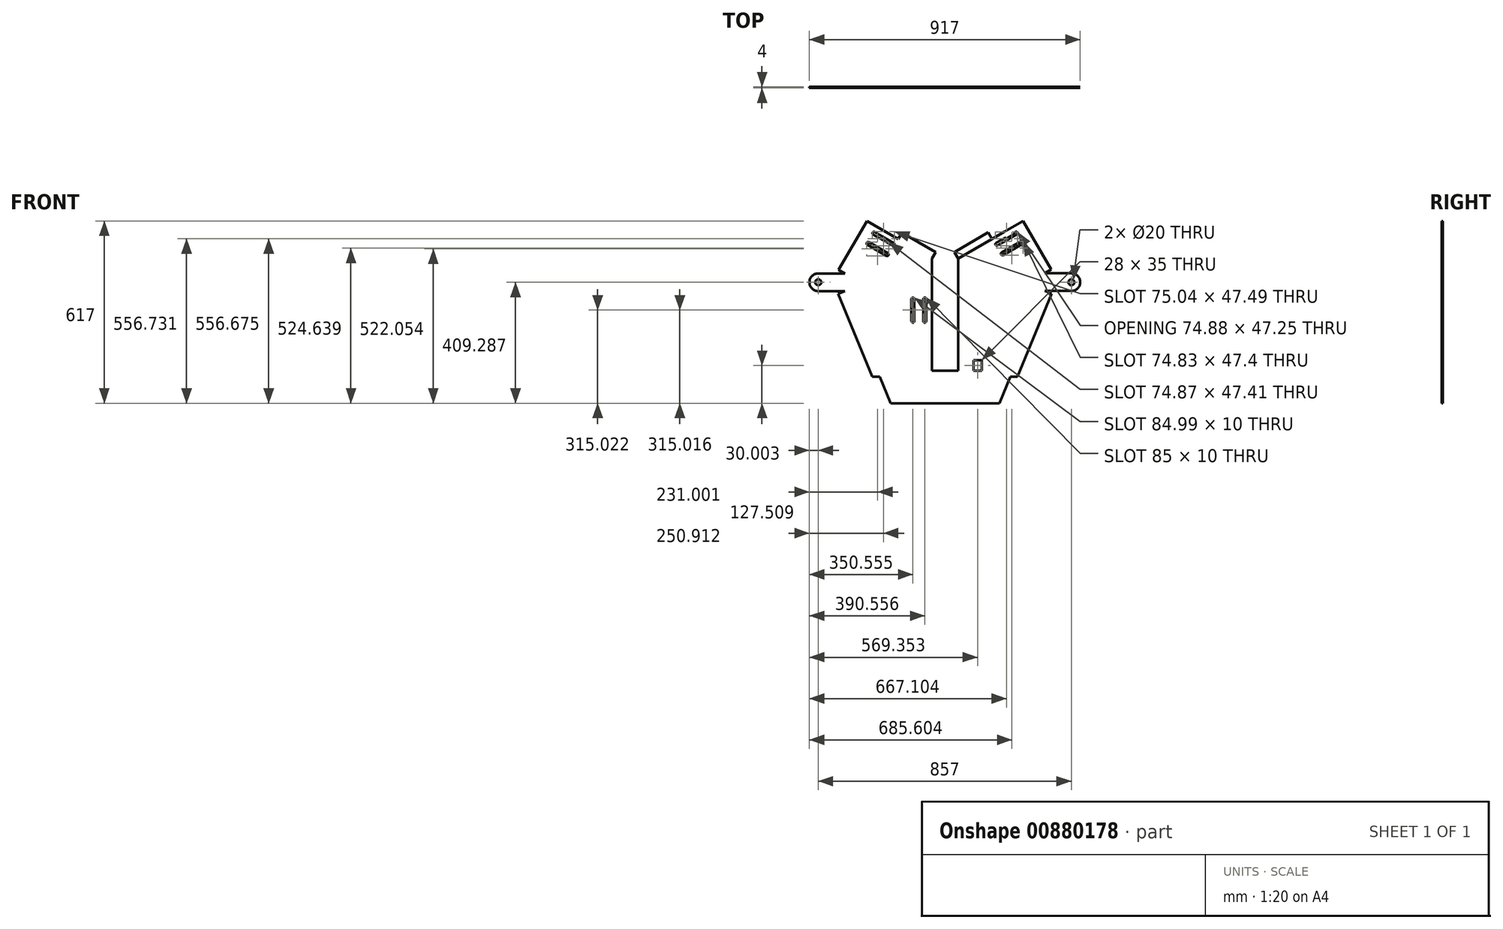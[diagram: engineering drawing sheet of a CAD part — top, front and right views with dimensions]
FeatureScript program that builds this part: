
annotation { "Feature Type Name" : "Feature", "Feature Type Description" : "" }
export const myFeature = defineFeature(function(context is Context, id is Id, definition is map)
    precondition{}
    {
        {
            var Q0;
            Q0=qCreatedBy(makeId("Front.planeOp"),FACE);
            var sketch = newSketch(context, id + "F0", { "sketchPlane" : qUnion([Q0])});
            skLineSegment(sketch, "E0", {"start": v(-22.56, -280.39) * mm, "end": v(-22.56, 69.61) * mm});
            skLineSegment(sketch, "E1", {"start": v(66.44, 119.61) * mm, "end": v(66.44, -280.39) * mm});
            skLineSegment(sketch, "E2", {"start": v(-174.12, 207.1) * mm, "end": v(-224.12, 120.5) * mm});
            skCircle(sketch, "E3", {"center": v(-218.75, 205.12) * mm, "radius": 5 * mm});
            skCircle(sketch, "E4", {"center": v(-153.63, 167.56) * mm, "radius": 5 * mm});
            skCircle(sketch, "E5", {"center": v(-238.59, 170.41) * mm, "radius": 5 * mm});
            skCircle(sketch, "E6", {"center": v(-173.63, 132.91) * mm, "radius": 5 * mm});
            skLineSegment(sketch, "E7", {"start": v(-171.13, 137.24) * mm, "end": v(-236.09, 174.74) * mm});
            skLineSegment(sketch, "E8", {"start": v(-241.09, 166.08) * mm, "end": v(-176.13, 128.58) * mm});
            skCircle(sketch, "E9", {"center": v(-46.56, -17.87) * mm, "radius": 5 * mm});
            skCircle(sketch, "E10", {"center": v(-46.56, -92.87) * mm, "radius": 5 * mm});
            skLineSegment(sketch, "E11", {"start": v(-51.55, -93.04) * mm, "end": v(-51.55, -17.7) * mm});
            skCircle(sketch, "E12", {"center": v(-86.56, -17.87) * mm, "radius": 5 * mm});
            skCircle(sketch, "E13", {"center": v(-86.56, -92.87) * mm, "radius": 5 * mm});
            skLineSegment(sketch, "E14", {"start": v(-81.6, -93.57) * mm, "end": v(-81.56, -17.87) * mm});
            skLineSegment(sketch, "E15", {"start": v(-91.56, -17.87) * mm, "end": v(-91.56, -92.87) * mm});
            skLineSegment(sketch, "E16", {"start": v(-41.56, -17.95) * mm, "end": v(-41.56, -92.7) * mm});
            skCircle(sketch, "E17", {"center": v(197.5, 167.6) * mm, "radius": 5 * mm});
            skCircle(sketch, "E18", {"center": v(262.46, 205.1) * mm, "radius": 5 * mm});
            skLineSegment(sketch, "E19", {"start": v(265.1, 200.86) * mm, "end": v(199.86, 163.19) * mm});
            skCircle(sketch, "E20", {"center": v(216.04, 135.5) * mm, "radius": 5 * mm});
            skCircle(sketch, "E21", {"center": v(281, 173) * mm, "radius": 5 * mm});
            skLineSegment(sketch, "E22", {"start": v(279.12, 177.65) * mm, "end": v(213.54, 139.84) * mm});
            skLineSegment(sketch, "E23", {"start": v(218.54, 131.18) * mm, "end": v(283.5, 168.68) * mm});
            skLineSegment(sketch, "E24", {"start": v(195.07, 171.97) * mm, "end": v(259.82, 209.34) * mm});
            skLineSegment(sketch, "E25", {"start": v(-102.56, -370.39) * mm, "end": v(146.44, -370.39) * mm});
            skLineSegment(sketch, "E26", {"start": v(359.9, 69.35) * mm, "end": v(359.9, 9.35) * mm});
            skLineSegment(sketch, "E27", {"start": v(-22.56, -260.39) * mm, "end": v(66.44, -260.39) * mm});
            skLineSegment(sketch, "E28", {"start": v(-22.56, 69.61) * mm, "end": v(-22.56, 119.61) * mm});
            skLineSegment(sketch, "E29", {"start": v(-177.57, 209.11) * mm, "end": v(-22.56, 119.61) * mm});
            skLineSegment(sketch, "E30", {"start": v(-22.56, 119.61) * mm, "end": v(66.44, 119.61) * mm});
            skLineSegment(sketch, "E31", {"start": v(-22.56, 119.61) * mm, "end": v(21.94, 196.69) * mm});
            skLineSegment(sketch, "E32", {"start": v(21.94, 196.69) * mm, "end": v(66.44, 119.61) * mm});
            skLineSegment(sketch, "E33", {"start": v(-0.3, 158.15) * mm, "end": v(66.44, 119.61) * mm});
            skLineSegment(sketch, "E34", {"start": v(44.2, 158.15) * mm, "end": v(-22.56, 119.61) * mm});
            skLineSegment(sketch, "E35", {"start": v(21.94, 119.61) * mm, "end": v(21.94, 196.69) * mm});
            skCircle(sketch, "E36", {"center": v(21.94, 145.3) * mm, "radius": 36.15 * mm});
            skLineSegment(sketch, "E37", {"start": v(-22.56, 119.61) * mm, "end": v(-174.1, 207.11) * mm});
            skLineSegment(sketch, "E38", {"start": v(-177.57, 209.11) * mm, "end": v(-220.88, 234.11) * mm});
            skLineSegment(sketch, "E39", {"start": v(-220.88, 234.11) * mm, "end": v(-317.1, 68.9) * mm, "construction": true});
            skLineSegment(sketch, "E40", {"start": v(146.44, -370.39) * mm, "end": v(206.44, -370.39) * mm});
            skLineSegment(sketch, "E41", {"start": v(-102.56, -370.39) * mm, "end": v(-162.56, -370.39) * mm});
            skLineSegment(sketch, "E42", {"start": v(66.44, 119.61) * mm, "end": v(221.46, 209.11) * mm});
            skLineSegment(sketch, "E43", {"start": v(221.46, 209.11) * mm, "end": v(264.76, 234.11) * mm});
            skLineSegment(sketch, "E44", {"start": v(264.76, 234.11) * mm, "end": v(359.9, 69.35) * mm});
            skLineSegment(sketch, "E45", {"start": v(359.9, 69.35) * mm, "end": v(419.9, 69.35) * mm});
            skLineSegment(sketch, "E46", {"start": v(419.9, 69.35) * mm, "end": v(419.9, 9.35) * mm});
            skLineSegment(sketch, "E47", {"start": v(419.9, 9.35) * mm, "end": v(359.9, 9.35) * mm});
            skLineSegment(sketch, "E48", {"start": v(359.9, 9.35) * mm, "end": v(206.44, -370.39) * mm});
            skLineSegment(sketch, "E49", {"start": v(-22.56, 119.61) * mm, "end": v(-22.56, -280.39) * mm});
            skLineSegment(sketch, "E50", {"start": v(-46.56, -17.87) * mm, "end": v(-46.56, -92.87) * mm});
            skLineSegment(sketch, "E51", {"start": v(-46.56, -55.37) * mm, "end": v(-86.28, -55.37) * mm});
            skPoint(sketch, "E51.endSnap0", {"position": v(-51.55, -93.87) * mm});
            skLineSegment(sketch, "E52", {"start": v(-46.56, -55.37) * mm, "end": v(-22.56, -55.37) * mm});
            skLineSegment(sketch, "E53", {"start": v(197.5, 167.6) * mm, "end": v(262.46, 205.1) * mm});
            skLineSegment(sketch, "E54", {"start": v(229.99, 186.35) * mm, "end": v(217.99, 207.13) * mm});
            skLineSegment(sketch, "E55", {"start": v(66.44, 119.61) * mm, "end": v(218, 207.11) * mm});
            skLineSegment(sketch, "E56", {"start": v(-3.49, 119.61) * mm, "end": v(47.38, 119.61) * mm});
            skLineSegment(sketch, "E57", {"start": v(-221.12, 200.72) * mm, "end": v(-156.13, 163.22) * mm});
            skLineSegment(sketch, "E58", {"start": v(-153.63, 167.56) * mm, "end": v(-151.13, 171.89) * mm});
            skLineSegment(sketch, "E59", {"start": v(-151.13, 171.89) * mm, "end": v(-216.25, 209.46) * mm});
            skLineSegment(sketch, "E60", {"start": v(-317.1, 68.9) * mm, "end": v(-317.1, 8.9) * mm});
            skLineSegment(sketch, "E61", {"start": v(-317.1, 8.9) * mm, "end": v(-162.56, -370.39) * mm});
            skLineSegment(sketch, "E62", {"start": v(-317.1, 68.9) * mm, "end": v(-377.1, 68.9) * mm});
            skLineSegment(sketch, "E63", {"start": v(-377.1, 68.9) * mm, "end": v(-377.1, 8.9) * mm});
            skLineSegment(sketch, "E64", {"start": v(-377.1, 8.9) * mm, "end": v(-317.1, 8.9) * mm});
            skLineSegment(sketch, "E65", {"start": v(66.44, 119.61) * mm, "end": v(66.44, -55.39) * mm});
            skLineSegment(sketch, "E66", {"start": v(66.44, -55.39) * mm, "end": v(-22.56, -55.39) * mm});
            skLineSegment(sketch, "E67", {"start": v(-22.56, -280.39) * mm, "end": v(-199.23, -280.39) * mm});
            skLineSegment(sketch, "E68", {"start": v(-199.23, -280.39) * mm, "end": v(242.81, -280.39) * mm});
            skLineSegment(sketch, "E69", {"start": v(242.81, -280.39) * mm, "end": v(267.81, -280.39) * mm});
            skLineSegment(sketch, "E70", {"start": v(359.9, 9.35) * mm, "end": v(383.07, -0.02) * mm});
            skLineSegment(sketch, "E71", {"start": v(267.81, -280.39) * mm, "end": v(383.07, -0.02) * mm});
            skLineSegment(sketch, "E72", {"start": v(-317.1, 8.9) * mm, "end": v(-340.26, -0.54) * mm});
            skLineSegment(sketch, "E73", {"start": v(-199.23, -280.39) * mm, "end": v(-224.23, -280.39) * mm});
            skLineSegment(sketch, "E74", {"start": v(-224.23, -280.39) * mm, "end": v(-340.26, -0.54) * mm});
            skLineSegment(sketch, "E75", {"start": v(-220.88, 234.11) * mm, "end": v(-242.53, 246.61) * mm});
            skLineSegment(sketch, "E76", {"start": v(-317.1, 68.9) * mm, "end": v(-338.7, 81.48) * mm});
            skLineSegment(sketch, "E77", {"start": v(-338.7, 81.48) * mm, "end": v(-242.53, 246.61) * mm});
            skLineSegment(sketch, "E78", {"start": v(-377.1, 8.9) * mm, "end": v(-437.1, 8.9) * mm});
            skLineSegment(sketch, "E79", {"start": v(-437.1, 8.9) * mm, "end": v(-437.1, 68.9) * mm});
            skLineSegment(sketch, "E80", {"start": v(-437.1, 68.9) * mm, "end": v(-377.1, 68.9) * mm});
            skPoint(sketch, "E81.centerSnap0", {"position": v(-437.1, 38.9) * mm});
            skPoint(sketch, "E81.centerSnap1", {"position": v(-407.1, 68.9) * mm});
            skLineSegment(sketch, "E82", {"start": v(66.44, 119.61) * mm, "end": v(264.76, 234.11) * mm});
            skLineSegment(sketch, "E83", {"start": v(264.76, 234.11) * mm, "end": v(286.42, 246.61) * mm});
            skLineSegment(sketch, "E84", {"start": v(286.42, 246.61) * mm, "end": v(381.54, 81.85) * mm});
            skLineSegment(sketch, "E85", {"start": v(381.54, 81.85) * mm, "end": v(359.9, 69.35) * mm});
            skLineSegment(sketch, "E86", {"start": v(419.9, 9.35) * mm, "end": v(479.9, 9.35) * mm});
            skLineSegment(sketch, "E87", {"start": v(479.9, 9.35) * mm, "end": v(479.9, 68.9) * mm});
            skLineSegment(sketch, "E88", {"start": v(479.9, 68.9) * mm, "end": v(419.9, 69.35) * mm});
            skLineSegment(sketch, "E89", {"start": v(-22.56, 119.61) * mm, "end": v(-10.06, 141.26) * mm});
            skLineSegment(sketch, "E90", {"start": v(-171.13, 128.58) * mm, "end": v(-136.96, 185.67) * mm});
            skLineSegment(sketch, "E91", {"start": v(-136.96, 185.67) * mm, "end": v(-124.46, 207.32) * mm});
            skLineSegment(sketch, "E92", {"start": v(-124.46, 207.32) * mm, "end": v(-10.06, 141.26) * mm});
            skLineSegment(sketch, "E93", {"start": v(211.63, 133.15) * mm, "end": v(181.19, 185.86) * mm});
            skLineSegment(sketch, "E94", {"start": v(181.19, 185.86) * mm, "end": v(168.69, 207.5) * mm});
            skLineSegment(sketch, "E95", {"start": v(168.69, 207.5) * mm, "end": v(53.94, 141.26) * mm});
            skLineSegment(sketch, "E96", {"start": v(53.94, 141.26) * mm, "end": v(66.44, 119.61) * mm});
            skCircle(sketch, "E97", {"center": v(-407.1, 38.9) * mm, "radius": 10 * mm});
            skCircle(sketch, "E98", {"center": v(449.9, 38.9) * mm, "radius": 10 * mm});
            skPoint(sketch, "E98.centerSnap0", {"position": v(449.9, 69.12) * mm});
            skSolve(sketch);
        }
        {
            var Q0;
            {var subQ4=sQuery(id+"F0.wireOp",EDGE,"E40");Q0=makeQuery(id+"F0.imprint","IMPRINT",FACE,{"disambiguationData":[TD([[makeQuery(id+"F0.imprint","IMPRINT",EDGE,{"derivedFrom":subQ4}),1.0]])]});}
            var Q1;
            Q1=makeQuery(id+"F0.imprint","IMPRINT",FACE,{"disambiguationData":[TD([[makeQuery(id+"F0.imprint","IMPRINT",EDGE,{"derivedFrom":sQuery(id+"F0.wireOp",EDGE,"E26")}),1.0]])]});
            var Q2;
            {var subQ18=sQuery(id+"F0.wireOp",EDGE,"E43");Q2=makeQuery(id+"F0.imprint","IMPRINT",FACE,{"disambiguationData":[TD([[makeQuery(id+"F0.imprint","IMPRINT",EDGE,{"derivedFrom":subQ18}),-1.0]])]});}
            var Q3;
            {var subQ14=sQuery(id+"F0.wireOp",EDGE,"25ec950b-0171-4492-b450-3eec572b7e29");Q3=makeQuery(id+"F0.imprint","IMPRINT",FACE,{"disambiguationData":[TD([[makeQuery(id+"F0.imprint","IMPRINT",EDGE,{"derivedFrom":subQ14}),1.0]])]});}
            var Q4;
            {var subQ4=sQuery(id+"F0.wireOp",EDGE,"1625b020-9225-42e4-9fd1-c3bdf133ad8f");Q4=makeQuery(id+"F0.imprint","IMPRINT",FACE,{"disambiguationData":[TD([[makeQuery(id+"F0.imprint","IMPRINT",EDGE,{"derivedFrom":subQ4}),-1.0]])]});}
            var Q5;
            {var subQ0=sQuery(id+"F0.wireOp",EDGE,"2095d209-febb-4da7-b659-262dc5fe09d2");Q5=makeQuery(id+"F0.imprint","IMPRINT",FACE,{"disambiguationData":[TD([[makeQuery(id+"F0.imprint","IMPRINT",EDGE,{"derivedFrom":subQ0}),-1.0]])]});}
            var Q6;
            {var subQ0=sQuery(id+"F0.wireOp",EDGE,"E57");var subQ1=sQuery(id+"F0.wireOp",EDGE,"E2");var subQ2=makeQuery(id+"F0.imprint","INTERSECT",VERTEX,{"derivedFrom":[subQ1,subQ0]});Q6=makeQuery(id+"F0.imprint","IMPRINT",FACE,{"disambiguationData":[TD([[makeQuery(id+"F0.imprint","IMPRINT",EDGE,{"disambiguationData":[TD([[subQ2,-1.0]])],"derivedFrom":subQ1}),-1.0]])]});}
            var Q7;
            {var subQ0=sQuery(id+"F0.wireOp",EDGE,"E54");var subQ1=sQuery(id+"F0.wireOp",EDGE,"E24");var subQ2=makeQuery(id+"F0.imprint","INTERSECT",VERTEX,{"derivedFrom":[subQ1,subQ0]});Q7=makeQuery(id+"F0.imprint","IMPRINT",FACE,{"disambiguationData":[TD([[makeQuery(id+"F0.imprint","IMPRINT",EDGE,{"disambiguationData":[TD([[subQ2,-1.0]])],"derivedFrom":subQ1}),1.0]])]});}
            var Q8;
            Q8=makeQuery(id+"F0.imprint","IMPRINT",FACE,{"disambiguationData":[TD([[makeQuery(id+"F0.imprint","IMPRINT",EDGE,{"derivedFrom":sQuery(id+"F0.wireOp",EDGE,"E60")}),-1.0]])]});
            var Q9;
            Q9=makeQuery(id+"F0.imprint","IMPRINT",FACE,{"disambiguationData":[TD([[makeQuery(id+"F0.imprint","IMPRINT",EDGE,{"derivedFrom":sQuery(id+"F0.wireOp",EDGE,"E63")}),-1.0]])]});
            var Q10;
            {var subQ2=sQuery(id+"F0.wireOp",EDGE,"E69");Q10=makeQuery(id+"F0.imprint","IMPRINT",FACE,{"disambiguationData":[TD([[makeQuery(id+"F0.imprint","IMPRINT",EDGE,{"derivedFrom":subQ2}),1.0]])]});}
            var Q11;
            Q11=makeQuery(id+"F0.imprint","IMPRINT",FACE,{"disambiguationData":[TD([[makeQuery(id+"F0.imprint","IMPRINT",EDGE,{"derivedFrom":sQuery(id+"F0.wireOp",EDGE,"E46")}),1.0]])]});
            var Q12;
            Q12=makeQuery(id+"F0.imprint","IMPRINT",FACE,{"disambiguationData":[TD([[makeQuery(id+"F0.imprint","IMPRINT",EDGE,{"derivedFrom":sQuery(id+"F0.wireOp",EDGE,"E44")}),1.0]])]});
            var Q13;
            Q13=makeQuery(id+"F0.imprint","IMPRINT",FACE,{"disambiguationData":[TD([[makeQuery(id+"F0.imprint","IMPRINT",EDGE,{"derivedFrom":sQuery(id+"F0.wireOp",EDGE,"E39")}),-1.0]])]});
            var Q14;
            {var subQ0=sQuery(id+"F0.wireOp",EDGE,"E72");Q14=makeQuery(id+"F0.imprint","IMPRINT",FACE,{"disambiguationData":[TD([[makeQuery(id+"F0.imprint","IMPRINT",EDGE,{"derivedFrom":subQ0}),1.0]])]});}
            var Q15;
            {var subQ0=sQuery(id+"F0.wireOp",EDGE,"E91");Q15=makeQuery(id+"F0.imprint","IMPRINT",FACE,{"disambiguationData":[TD([[makeQuery(id+"F0.imprint","IMPRINT",EDGE,{"derivedFrom":subQ0}),-1.0]])]});}
            var Q16;
            {var subQ0=sQuery(id+"F0.wireOp",EDGE,"E92");var subQ1=sQuery(id+"F0.wireOp",EDGE,"E36");var subQ2=makeQuery(id+"F0.imprint","INTERSECT",VERTEX,{"derivedFrom":[subQ1,subQ0]});Q16=makeQuery(id+"F0.imprint","IMPRINT",FACE,{"disambiguationData":[TD([[makeQuery(id+"F0.imprint","IMPRINT",EDGE,{"disambiguationData":[TD([[subQ2,-1.0]])],"derivedFrom":subQ1}),1.0]])]});}
            var Q17;
            {var subQ1=sQuery(id+"F0.wireOp",EDGE,"E94");Q17=makeQuery(id+"F0.imprint","IMPRINT",FACE,{"disambiguationData":[TD([[makeQuery(id+"F0.imprint","IMPRINT",EDGE,{"derivedFrom":subQ1}),1.0]])]});}
            var Q18;
            {var subQ1=sQuery(id+"F0.wireOp",EDGE,"E24");var subQ8=sQuery(id+"F0.wireOp",EDGE,"E17");var subQ10=makeQuery(id+"F0.imprint","INTERSECT",VERTEX,{"derivedFrom":[subQ8,subQ1]});Q18=makeQuery(id+"F0.imprint","IMPRINT",FACE,{"disambiguationData":[TD([[makeQuery(id+"F0.imprint","IMPRINT",EDGE,{"disambiguationData":[TD([[subQ10,-1.0]])],"derivedFrom":subQ8}),-1.0]])]});}
            var Q19;
            {var subQ0=sQuery(id+"F0.wireOp",EDGE,"E95");var subQ1=sQuery(id+"F0.wireOp",EDGE,"E36");var subQ2=makeQuery(id+"F0.imprint","INTERSECT",VERTEX,{"derivedFrom":[subQ1,subQ0]});Q19=makeQuery(id+"F0.imprint","IMPRINT",FACE,{"disambiguationData":[TD([[makeQuery(id+"F0.imprint","IMPRINT",EDGE,{"disambiguationData":[TD([[subQ2,1.0]])],"derivedFrom":subQ1}),1.0]])]});}
            extrude(context, id + "F1", {"entities" : qUnion([Q0, Q1, Q2, Q3, Q4, Q5, Q6, Q7, Q8, Q9, Q10, Q11, Q12, Q13, Q14, Q15, Q16, Q17, Q18, Q19]), "depth" : 4 * mm, "offsetDistance" : 25 * mm});
        }
        {
            var Q0;
            Q0=makeQuery(id+"F1.opExtrude","SWEPT_EDGE",EDGE,{"disambiguationData":[OSD([sQuery(id+"F0.wireOp",EDGE,"E79"),sQuery(id+"F0.wireOp",EDGE,"E80")])]});
            var Q1;
            Q1=makeQuery(id+"F1.opExtrude","SWEPT_EDGE",EDGE,{"disambiguationData":[OSD([sQuery(id+"F0.wireOp",EDGE,"E78"),sQuery(id+"F0.wireOp",EDGE,"E79")])]});
            fillet(context, id + "F2", {"entities" : qUnion([Q0, Q1]), "radius" : 30 * mm, "tangentPropagation" : true, "allowEdgeOverflow" : false});
        }
        {
            var Q0;
            Q0=makeQuery(id+"F1.opExtrude","SWEPT_EDGE",EDGE,{"disambiguationData":[OSD([sQuery(id+"F0.wireOp",EDGE,"E86"),sQuery(id+"F0.wireOp",EDGE,"E87")])]});
            var Q1;
            Q1=makeQuery(id+"F1.opExtrude","SWEPT_EDGE",EDGE,{"disambiguationData":[OSD([sQuery(id+"F0.wireOp",EDGE,"E87"),sQuery(id+"F0.wireOp",EDGE,"E88")])]});
            fillet(context, id + "F3", {"entities" : qUnion([Q0, Q1]), "radius" : 30 * mm, "tangentPropagation" : true, "allowEdgeOverflow" : false});
        }
        {
            var Q0;
            {var subQ3=sQuery(id+"F0.wireOp",EDGE,"E2");var subQ7=sQuery(id+"F0.wireOp",EDGE,"E57");var subQ11=makeQuery(id+"F0.imprint","INTERSECT",VERTEX,{"derivedFrom":[subQ3,subQ7]});Q0=makeQuery(id+"F0.imprint","IMPRINT",FACE,{"disambiguationData":[TD([[makeQuery(id+"F0.imprint","IMPRINT",EDGE,{"disambiguationData":[TD([[subQ11,-1.0]])],"derivedFrom":subQ3}),1.0]])]});}
            extrude(context, id + "F4", {"entities" : qUnion([Q0]), "operationType" : NewBodyOperationType.ADD, "depth" : 4 * mm, "offsetDistance" : 25 * mm});
        }
        {
            var Q0;
            {var subQ3=sQuery(id+"F0.wireOp",EDGE,"E27");Q0=makeQuery(id+"F0.imprint","IMPRINT",FACE,{"disambiguationData":[TD([[makeQuery(id+"F0.imprint","IMPRINT",EDGE,{"derivedFrom":subQ3}),-1.0]])]});}
            extrude(context, id + "F5", {"entities" : qUnion([Q0]), "operationType" : NewBodyOperationType.ADD, "depth" : 4 * mm, "offsetDistance" : 25 * mm});
        }
        {
            var Q0;
            {var subQ0=sQuery(id+"F0.wireOp",EDGE,"E68");var subQ1=sQuery(id+"F0.wireOp",EDGE,"E49");var subQ2=sQuery(id+"F0.wireOp",EDGE,"E1");var subQ3=sQuery(id+"F0.wireOp",EDGE,"E90");var subQ4=sQuery(id+"F0.wireOp",EDGE,"E57");var subQ5=sQuery(id+"F0.wireOp",EDGE,"E7");var subQ6=sQuery(id+"F0.wireOp",EDGE,"E6");var subQ7=sQuery(id+"F0.wireOp",EDGE,"E4");var subQ8=sQuery(id+"F0.wireOp",EDGE,"E2");Q0=makeQuery(id+"F5.boolean.opBoolean","MERGE",FACE,{"derivedFrom":[makeQuery(id+"F4.boolean.opBoolean","MERGE",FACE,{"derivedFrom":[makeQuery(id+"F1.opExtrude","CAP_FACE",FACE,{"disambiguationData":[OSD([subQ2,subQ8,sQuery(id+"F0.wireOp",EDGE,"E3"),subQ7,sQuery(id+"F0.wireOp",EDGE,"E5"),subQ6,subQ5,sQuery(id+"F0.wireOp",EDGE,"E8"),sQuery(id+"F0.wireOp",EDGE,"E9"),sQuery(id+"F0.wireOp",EDGE,"E10"),sQuery(id+"F0.wireOp",EDGE,"E11"),sQuery(id+"F0.wireOp",EDGE,"E12"),sQuery(id+"F0.wireOp",EDGE,"E13"),sQuery(id+"F0.wireOp",EDGE,"E14"),sQuery(id+"F0.wireOp",EDGE,"E15"),sQuery(id+"F0.wireOp",EDGE,"E16"),sQuery(id+"F0.wireOp",EDGE,"E17"),sQuery(id+"F0.wireOp",EDGE,"E18"),sQuery(id+"F0.wireOp",EDGE,"E19"),sQuery(id+"F0.wireOp",EDGE,"E20"),sQuery(id+"F0.wireOp",EDGE,"E21"),sQuery(id+"F0.wireOp",EDGE,"E22"),sQuery(id+"F0.wireOp",EDGE,"E23"),sQuery(id+"F0.wireOp",EDGE,"E24"),sQuery(id+"F0.wireOp",EDGE,"E25"),sQuery(id+"F0.wireOp",EDGE,"E29"),sQuery(id+"F0.wireOp",EDGE,"E37"),sQuery(id+"F0.wireOp",EDGE,"E38"),sQuery(id+"F0.wireOp",EDGE,"E40"),sQuery(id+"F0.wireOp",EDGE,"E41"),sQuery(id+"F0.wireOp",EDGE,"E42"),sQuery(id+"F0.wireOp",EDGE,"E45"),sQuery(id+"F0.wireOp",EDGE,"E47"),sQuery(id+"F0.wireOp",EDGE,"E48"),subQ1,subQ4,sQuery(id+"F0.wireOp",EDGE,"E59"),sQuery(id+"F0.wireOp",EDGE,"E61"),sQuery(id+"F0.wireOp",EDGE,"E62"),sQuery(id+"F0.wireOp",EDGE,"E64"),sQuery(id+"F0.wireOp",EDGE,"E65"),subQ0,sQuery(id+"F0.wireOp",EDGE,"E69"),sQuery(id+"F0.wireOp",EDGE,"E70"),sQuery(id+"F0.wireOp",EDGE,"E71"),sQuery(id+"F0.wireOp",EDGE,"E72"),sQuery(id+"F0.wireOp",EDGE,"E73"),sQuery(id+"F0.wireOp",EDGE,"E74"),sQuery(id+"F0.wireOp",EDGE,"E75"),sQuery(id+"F0.wireOp",EDGE,"E76"),sQuery(id+"F0.wireOp",EDGE,"E77"),sQuery(id+"F0.wireOp",EDGE,"E78"),sQuery(id+"F0.wireOp",EDGE,"E79"),sQuery(id+"F0.wireOp",EDGE,"E80"),sQuery(id+"F0.wireOp",EDGE,"E82"),sQuery(id+"F0.wireOp",EDGE,"E83"),sQuery(id+"F0.wireOp",EDGE,"E84"),sQuery(id+"F0.wireOp",EDGE,"E85"),sQuery(id+"F0.wireOp",EDGE,"E86"),sQuery(id+"F0.wireOp",EDGE,"E87"),sQuery(id+"F0.wireOp",EDGE,"E88"),sQuery(id+"F0.wireOp",EDGE,"E89"),subQ3,sQuery(id+"F0.wireOp",EDGE,"E91"),sQuery(id+"F0.wireOp",EDGE,"E92"),sQuery(id+"F0.wireOp",EDGE,"E94"),sQuery(id+"F0.wireOp",EDGE,"E95"),sQuery(id+"F0.wireOp",EDGE,"E96"),sQuery(id+"F0.wireOp",EDGE,"E97"),sQuery(id+"F0.wireOp",EDGE,"E98")])],"isStart":false}),makeQuery(id+"F4.opExtrude","CAP_FACE",FACE,{"disambiguationData":[OSD([subQ8,subQ7,subQ6,subQ5,subQ4,subQ3])],"isStart":false})]}),makeQuery(id+"F5.opExtrude","CAP_FACE",FACE,{"disambiguationData":[OSD([subQ2,sQuery(id+"F0.wireOp",EDGE,"E27"),subQ1,subQ0])],"isStart":false})]});}
            var sketch = newSketch(context, id + "F6", { "sketchPlane" : qUnion([Q0])});
            skLineSegment(sketch, "E99", {"start": v(31.16, -63.4) * mm, "end": v(23.64, -63.4) * mm});
            skLineSegment(sketch, "E100", {"start": v(23.64, -63.4) * mm, "end": v(23.64, -73.4) * mm});
            skLineSegment(sketch, "E101", {"start": v(23.64, -73.4) * mm, "end": v(5.64, -73.4) * mm});
            skLineSegment(sketch, "E102", {"start": v(23.64, -73.4) * mm, "end": v(33.64, -73.4) * mm});
            skLineSegment(sketch, "E103", {"start": v(33.64, -73.4) * mm, "end": v(33.64, -58.4) * mm});
            skLineSegment(sketch, "E104", {"start": v(23.64, -63.4) * mm, "end": v(5.64, -63.4) * mm});
            skLineSegment(sketch, "E105", {"start": v(5.64, -63.4) * mm, "end": v(5.64, -83.4) * mm});
            skLineSegment(sketch, "E106", {"start": v(5.64, -83.4) * mm, "end": v(33.64, -83.4) * mm});
            skLineSegment(sketch, "E107", {"start": v(33.64, -83.4) * mm, "end": v(33.64, -73.4) * mm});
            skLineSegment(sketch, "E108", {"start": v(31.16, -63.4) * mm, "end": v(33.64, -63.4) * mm});
            skLineSegment(sketch, "E109", {"start": v(33.64, -63.4) * mm, "end": v(33.64, -53.4) * mm});
            skLineSegment(sketch, "E110", {"start": v(33.64, -53.4) * mm, "end": v(5.64, -53.4) * mm});
            skLineSegment(sketch, "E111", {"start": v(5.64, -53.4) * mm, "end": v(5.64, -63.4) * mm});
            skLineSegment(sketch, "E112", {"start": v(33.64, -53.4) * mm, "end": v(33.64, -48.4) * mm});
            skLineSegment(sketch, "E113", {"start": v(33.64, -48.4) * mm, "end": v(5.64, -48.4) * mm});
            skLineSegment(sketch, "E114", {"start": v(5.64, -48.4) * mm, "end": v(5.64, -53.4) * mm});
            skSolve(sketch);
        }
        {
            var Q0;
            Q0=makeQuery(id+"F6.imprint","IMPRINT",FACE,{"disambiguationData":[TD([[makeQuery(id+"F6.imprint","IMPRINT",EDGE,{"derivedFrom":sQuery(id+"F6.wireOp",EDGE,"E110")}),-1.0]])]});
            var sketch = newSketch(context, id + "F7", { "sketchPlane" : qUnion([Q0])});
            skLineSegment(sketch, "E115", {"start": v(143.76, -240.38) * mm, "end": v(136.24, -240.38) * mm});
            skLineSegment(sketch, "E116", {"start": v(136.24, -240.38) * mm, "end": v(136.24, -250.38) * mm});
            skLineSegment(sketch, "E117", {"start": v(136.24, -250.38) * mm, "end": v(118.24, -250.38) * mm});
            skLineSegment(sketch, "E118", {"start": v(136.24, -250.38) * mm, "end": v(146.24, -250.38) * mm});
            skLineSegment(sketch, "E119", {"start": v(146.24, -250.38) * mm, "end": v(146.24, -235.38) * mm});
            skLineSegment(sketch, "E120", {"start": v(136.24, -240.38) * mm, "end": v(118.24, -240.38) * mm});
            skLineSegment(sketch, "E121", {"start": v(118.24, -240.38) * mm, "end": v(118.24, -260.38) * mm});
            skLineSegment(sketch, "E122", {"start": v(118.24, -260.38) * mm, "end": v(146.24, -260.38) * mm});
            skLineSegment(sketch, "E123", {"start": v(146.24, -260.38) * mm, "end": v(146.24, -250.38) * mm});
            skLineSegment(sketch, "E124", {"start": v(126.72, -240.38) * mm, "end": v(146.24, -240.38) * mm});
            skLineSegment(sketch, "E125", {"start": v(146.24, -240.38) * mm, "end": v(146.24, -230.38) * mm});
            skLineSegment(sketch, "E126", {"start": v(146.24, -230.38) * mm, "end": v(118.24, -230.38) * mm});
            skLineSegment(sketch, "E127", {"start": v(118.24, -230.38) * mm, "end": v(118.24, -240.38) * mm});
            skLineSegment(sketch, "E128", {"start": v(146.24, -230.38) * mm, "end": v(146.24, -225.38) * mm});
            skLineSegment(sketch, "E129", {"start": v(146.24, -225.38) * mm, "end": v(118.24, -225.38) * mm});
            skLineSegment(sketch, "E130", {"start": v(118.24, -225.38) * mm, "end": v(118.24, -230.38) * mm});
            skLineSegment(sketch, "E131", {"start": v(118.24, -260.38) * mm, "end": v(66.45, -260.38) * mm});
            skSolve(sketch);
        }
        {
            var Q0;
            Q0 = qSketchRegion(id + "F7", true);
            extrude(context, id + "F8", {"entities" : qUnion([Q0]), "operationType" : NewBodyOperationType.REMOVE, "oppositeDirection" : true, "depth" : 25 * mm, "offsetDistance" : 25 * mm});
        }
    });
